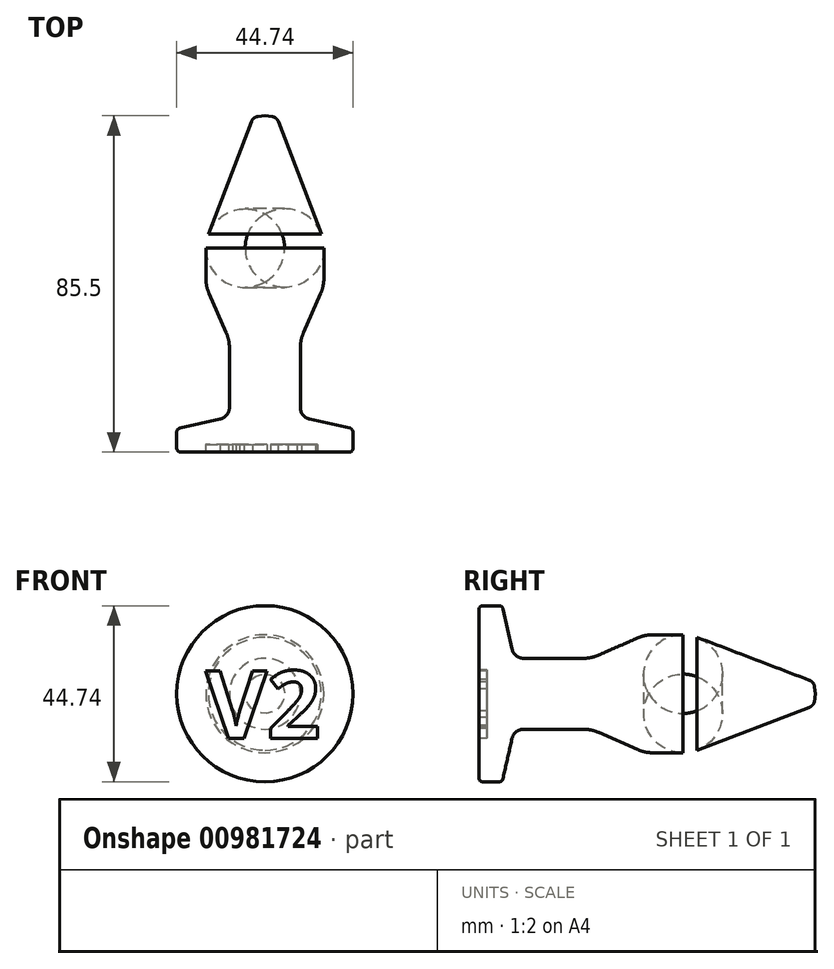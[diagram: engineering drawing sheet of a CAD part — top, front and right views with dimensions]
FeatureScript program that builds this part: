
annotation { "Feature Type Name" : "Feature", "Feature Type Description" : "" }
export const myFeature = defineFeature(function(context is Context, id is Id, definition is map)
    precondition{}
    {
        {
            var Q0;
            Q0=qCreatedBy(makeId("Top.planeOp"),FACE);
            var sketch = newSketch(context, id + "F0", { "sketchPlane" : qUnion([Q0])});
            skLineSegment(sketch, "E0", {"start": v(0, 0) * mm, "end": v(22.37, 0) * mm});
            skLineSegment(sketch, "E1", {"start": v(22.37, 0) * mm, "end": v(22.37, 5.93) * mm});
            skLineSegment(sketch, "E2", {"start": v(22.37, 5.93) * mm, "end": v(9, 8.97) * mm});
            skLineSegment(sketch, "E3", {"start": v(9, 8.97) * mm, "end": v(9, 28.54) * mm});
            skLineSegment(sketch, "E4", {"start": v(9, 28.54) * mm, "end": v(15, 42.2) * mm});
            skLineSegment(sketch, "E5", {"start": v(15, 42.2) * mm, "end": v(15, 53.7) * mm});
            skLineSegment(sketch, "E6", {"start": v(0, 74.82) * mm, "end": v(0, 0) * mm});
            skLineSegment(sketch, "E7", {"start": v(0, 85.5) * mm, "end": v(0, -9.47) * mm});
            skLineSegment(sketch, "E8", {"start": v(15, 53.7) * mm, "end": v(2.98, 85.16) * mm});
            skLineSegment(sketch, "E9", {"start": v(2.98, 85.16) * mm, "end": v(0, 85.5) * mm});
            skSolve(sketch);
        }
        {
            var Q0;
            Q0=qSketchRegion(id+"F0",true);
            var Q1;
            Q1=sQuery(id+"F0.wireOp",EDGE,"E7");
            revolve(context, id + "F1", {"surfaceOperationType" : NewSurfaceOperationType.NEW, "entities" : qUnion([Q0]), "axis" : qUnion([Q1]), "revolveType" : RevolveType.FULL});
        }
        {
            var Q0;
            Q0=makeQuery(id+"F1.opRevolve","SWEPT_EDGE",EDGE,{"disambiguationData":[OSD([sQuery(id+"F0.wireOp",EDGE,"E5"),sQuery(id+"F0.wireOp",EDGE,"wUMg07Op-mwMA-P6fm-YsAe-xgAx8nRf7R74")])]});
            var Q1;
            Q1=makeQuery(id+"F1.opRevolve","SWEPT_EDGE",EDGE,{"disambiguationData":[OSD([sQuery(id+"F0.wireOp",EDGE,"E4"),sQuery(id+"F0.wireOp",EDGE,"E5")])]});
            var Q2;
            Q2=makeQuery(id+"F1.opRevolve","SWEPT_EDGE",EDGE,{"disambiguationData":[OSD([sQuery(id+"F0.wireOp",EDGE,"E3"),sQuery(id+"F0.wireOp",EDGE,"E4")])]});
            fillet(context, id + "F2", {"entities" : qUnion([Q0, Q1, Q2]), "radius" : 10 * mm, "tangentPropagation" : true, "allowEdgeOverflow" : false});
        }
        {
            var Q0;
            Q0=makeQuery(id+"F1.opRevolve","SWEPT_EDGE",EDGE,{"disambiguationData":[OSD([sQuery(id+"F0.wireOp",EDGE,"E2"),sQuery(id+"F0.wireOp",EDGE,"E3")])]});
            fillet(context, id + "F3", {"entities" : qUnion([Q0]), "radius" : 3 * mm, "tangentPropagation" : true, "allowEdgeOverflow" : false});
        }
        {
            var Q0;
            Q0=makeQuery(id+"F1.opRevolve","SWEPT_EDGE",EDGE,{"disambiguationData":[OSD([sQuery(id+"F0.wireOp",EDGE,"E1"),sQuery(id+"F0.wireOp",EDGE,"E2")])]});
            var Q1;
            Q1=makeQuery(id+"F1.opRevolve","SWEPT_EDGE",EDGE,{"disambiguationData":[OSD([sQuery(id+"F0.wireOp",EDGE,"E0"),sQuery(id+"F0.wireOp",EDGE,"E1")])]});
            fillet(context, id + "F4", {"entities" : qUnion([Q0, Q1]), "radius" : 1 * mm, "tangentPropagation" : true, "allowEdgeOverflow" : false});
        }
        {
            var Q0;
            Q0=makeQuery(id+"F1.opRevolve","SWEPT_EDGE",EDGE,{"disambiguationData":[OSD([sQuery(id+"F0.wireOp",EDGE,"E8"),sQuery(id+"F0.wireOp",EDGE,"E9")])]});
            fillet(context, id + "F5", {"entities" : qUnion([Q0]), "radius" : 2 * mm, "tangentPropagation" : true, "allowEdgeOverflow" : false});
        }
        {
            var Q0;
            Q0=qCreatedBy(makeId("Front.planeOp"),FACE);
            var sketch = newSketch(context, id + "F6", { "sketchPlane" : qUnion([Q0])});
            skText(sketch, "E10", { "text": "V2", "fontName": "OpenSans-Bold.ttf"});
            const initialGuessF6  = {"E10": [-0.01506, -0.0113, 1, 0, 0.01723]};
            skSetInitialGuess(sketch, initialGuessF6);
            skSolve(sketch);
        }
        {
            var Q0;
            Q0=makeQuery(id+"F6.imprint","IMPRINT",FACE,{"disambiguationData":[TD([[makeQuery(id+"F6.imprint","IMPRINT",EDGE,{"derivedFrom":sQuery(id+"F6.wireOp",EDGE,"E10.sketch_text.stroke-0")}),-1.0]])]});
            var Q1;
            Q1=makeQuery(id+"F6.imprint","IMPRINT",FACE,{"disambiguationData":[TD([[makeQuery(id+"F6.imprint","IMPRINT",EDGE,{"derivedFrom":sQuery(id+"F6.wireOp",EDGE,"E10.sketch_text.stroke-12")}),-1.0]])]});
            var Q2;
            Q2=makeQuery(id+"F6.imprint","IMPRINT",FACE,{"disambiguationData":[TD([[makeQuery(id+"F6.imprint","IMPRINT",EDGE,{"derivedFrom":sQuery(id+"F6.wireOp",EDGE,"E10.sketch_text.stroke-20")}),-1.0]])]});
            extrude(context, id + "F7", {"entities" : qUnion([Q0, Q1, Q2]), "operationType" : NewBodyOperationType.REMOVE, "surfaceOperationType" : NewSurfaceOperationType.ADD, "oppositeDirection" : true, "depth" : 2 * mm, "offsetDistance" : 25 * mm});
        }
    });
